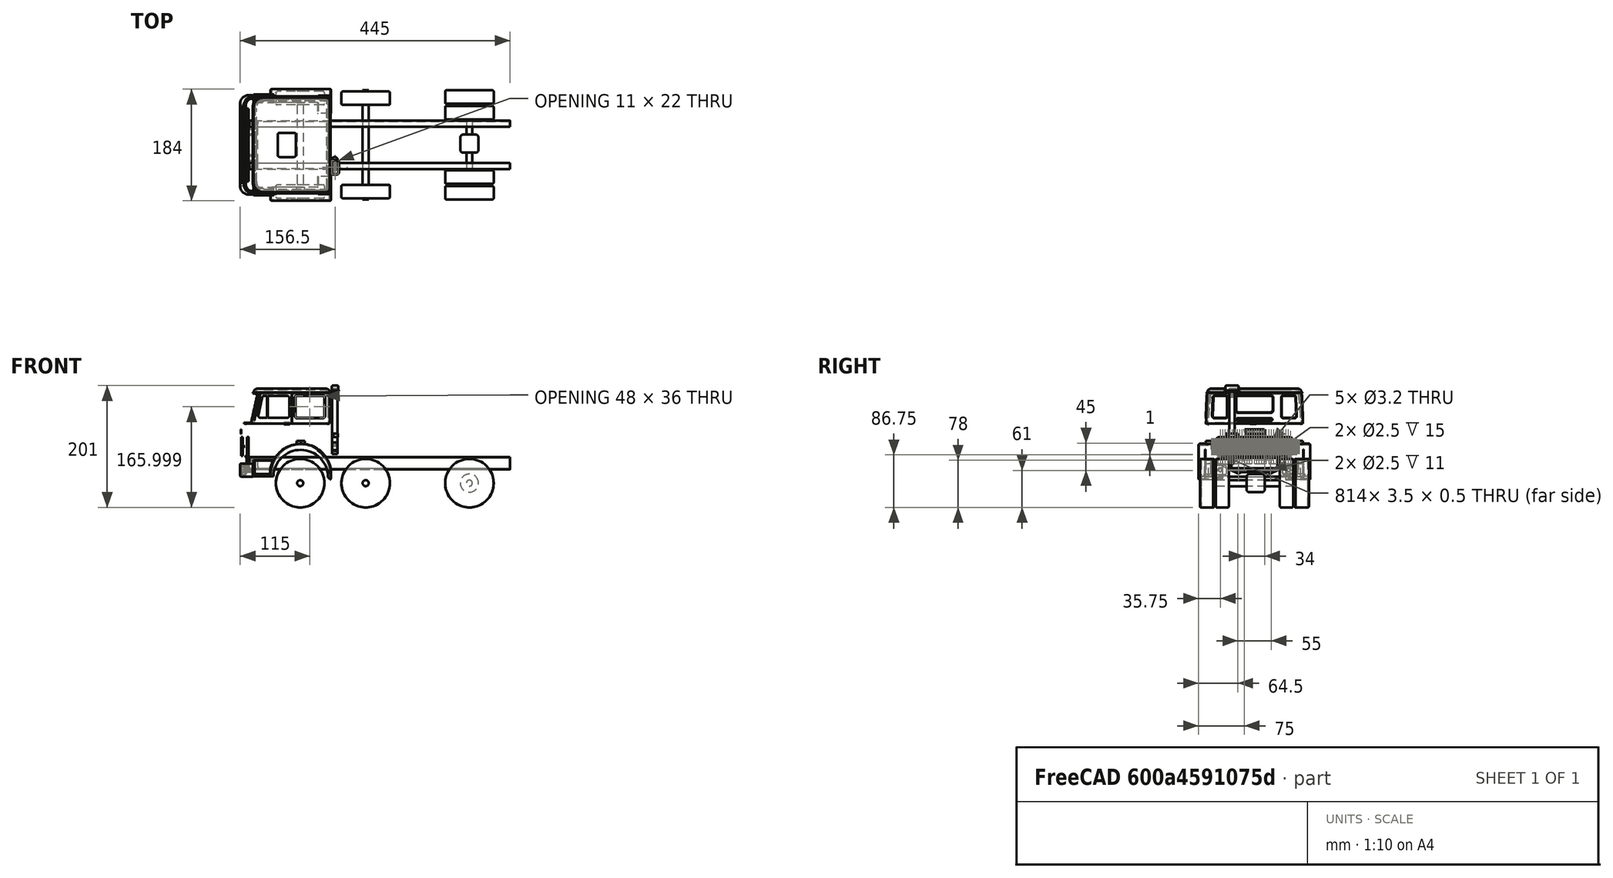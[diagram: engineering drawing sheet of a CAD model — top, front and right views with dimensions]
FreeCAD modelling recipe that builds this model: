
FCSTD DOCUMENT  (FreeCAD 0.20R)
Label: Cab-EMPTY-08a-splitted
License: CC-BY 3.0
LicenseURL: http://creativecommons.org/licenses/by/3.0/
objects: Part::Box×172, Part::Cut×85, Part::MultiFuse×76, Part::Fillet×54, Part::Cylinder×51, Part::Extrusion×7, Part::Mirroring×5, Part::Part2DObjectPython×5, Part::Feature×3, Part::Chamfer×2, Part::Torus×2
note: 462 computed .brp shape members not serialized (recipe doc carries the construction recipe); baked Part::Feature solids carry a one-line shape summary decoded from their .brp

FEATURE [Part::Cut] Cut
  Refine = true
FEATURE [Part::MultiFuse] Fusion
  Refine = true
FEATURE [Part::Cut] Cut001  label="cab"
  Base = -> Cut
  Refine = true
  Tool = -> Fusion
FEATURE [Part::Box] Box  label="Cube"
  AttacherType = Attacher::AttachEngine3D
  Height = 64
  Length = 150
  Placement = pos=(0,-1,-4) rot=(0,0,1;0rad)
  Width = 170
FEATURE [Part::Box] Box001  label="Cube001"
  AttacherType = Attacher::AttachEngine3D
  Height = 64
  Length = 150
  Placement = pos=(0,-1,60) rot=(0,0,1;0rad)
  Width = 170
FEATURE [Part::MultiFuse] Fusion001
  Refine = true
FEATURE [Part::Cut] Cut002
  Refine = true
FEATURE [Part::Cut] Cut004
  Base = -> Cut001
  Refine = true
  Tool = -> Box
FEATURE [Part::Box] Box002  label="Cube002"
  AttacherType = Attacher::AttachEngine3D
  Height = 2
  Length = 10
  Placement = pos=(70,7,59) rot=(0,0,1;0rad)
  Width = 1
FEATURE [Part::Box] Box003  label="Cube003"
  AttacherType = Attacher::AttachEngine3D
  Height = 2
  Length = 10
  Placement = pos=(70,160,59.5) rot=(0,0,1;0rad)
  Width = 1
FEATURE [Part::Box] Box004  label="Cube004"
  AttacherType = Attacher::AttachEngine3D
  Height = 2
  Length = 1
  Placement = pos=(142,77,59.5) rot=(0,0,1;0rad)
  Width = 10
FEATURE [Part::Box] Box005  label="Cube005"
  AttacherType = Attacher::AttachEngine3D
  Height = 2
  Length = 1
  Placement = pos=(7,77,59.5) rot=(0,0,1;0rad)
  Width = 10
FEATURE [Part::MultiFuse] Fusion002
  Refine = true
  Shapes = -> [Box002,Box005,Box004,Box003]
FEATURE [Part::MultiFuse] Fusion003
  Refine = true
  Shapes = -> [Cut004,Fusion002]
FEATURE [Part::Chamfer] Chamfer001
  Base = -> Fusion003
  Edges = 3 edges r=0.5: [Edge92,Edge231,Edge238]
FEATURE [Part::Chamfer] Chamfer
  Base = -> Chamfer001
  Edges = 1 edges r=0.5: [Edge236]
FEATURE [Part::Box] Box006  label="Cube006"
  AttacherType = Attacher::AttachEngine3D
  Height = 48
  Length = 30
  Placement = pos=(0,4,61.5) rot=(0,0,1;0rad)
  Width = 170
FEATURE [Part::Box] Box007  label="Cube007"
  AttacherType = Attacher::AttachEngine3D
  Height = 59
  Length = 15
  Placement = pos=(15.66,0,60) rot=(0,1,0;0.218166rad)
  Width = 180
FEATURE [Part::Cut] Cut006
  Base = -> Box006
  Refine = true
  Tool = -> Box007
FEATURE [Part::Fillet] Fillet
  Base = -> Cut006
  Edges = 1 edges r=1: [Edge9]
FEATURE [Part::Fillet] Fillet001
  Base = -> Fillet
  Edges = 1 edges r=1: [Edge8]
FEATURE [Part::Cut] Cut007
  Base = -> Chamfer
  Refine = true
  Tool = -> Fillet001
FEATURE [Part::Box] Box008  label="Cube008"
  AttacherType = Attacher::AttachEngine3D
  Height = 36
  Length = 36
  Placement = pos=(43,2,70) rot=(0,0,1;0rad)
  Width = 180
FEATURE [Part::Fillet] Fillet002
  Base = -> Box008
  Edges = 2 edges r=3: [Edge6,Edge8]
FEATURE [Part::Cut] Cut008
  Base = -> Cut007
  Refine = true
  Tool = -> Fillet002
FEATURE [Part::Box] Box009  label="Cube009"
  AttacherType = Attacher::AttachEngine3D
  Height = 36
  Length = 48
  Placement = pos=(89,2,70) rot=(0,0,1;0rad)
  Width = 180
FEATURE [Part::Fillet] Fillet003
  Base = -> Box009
  Edges = 4 edges r=3: [Edge2,Edge4,Edge6,Edge8]
FEATURE [Part::Cut] Cut009
  Base = -> Cut008
  Refine = true
  Tool = -> Fillet003
FEATURE [Part::Cut] Cut010
  Placement = pos=(0,1,1) rot=(0,0,1;0rad)
  Refine = true
FEATURE [Part::Fillet] Fillet004
  Base = -> Cut010
  Edges = 4 edges r=3: [Edge5,Edge7,Edge8,Edge11]
  Placement = pos=(-32.5,14,69) rot=(0,0,1;0rad)
FEATURE [Part::Cut] Cut011
  Placement = pos=(0,1,1) rot=(0,0,1;0rad)
  Refine = true
FEATURE [Part::Fillet] Fillet005
  Base = -> Cut011
  Edges = 4 edges r=3: [Edge5,Edge7,Edge8,Edge11]
  Placement = pos=(-32.5,14,69) rot=(0,0,1;0rad)
FEATURE [Part::Mirroring] Part__Mirroring  label="Fillet005 (Mirror #1)"
  Base = (0,0,0)
  Normal = (0,1,0)
  Placement = pos=(0,168,0) rot=(0,0,1;0rad)
  Source = -> Fillet005
FEATURE [Part::MultiFuse] Fusion004
  Refine = true
  Shapes = -> [Fillet004,Part__Mirroring]
FEATURE [Part::Cut] Cut012
  Base = -> Cut009
  Refine = true
  Tool = -> Fusion004
FEATURE [Part::Box] Box010  label="Cube010"
  AttacherType = Attacher::AttachEngine3D
  Height = 27
  Length = 10
  Placement = pos=(139,54,79) rot=(0,0,1;0rad)
  Width = 60
FEATURE [Part::Fillet] Fillet006
  Base = -> Box010
  Edges = 4 edges r=3: [Edge9,Edge10,Edge11,Edge12]
FEATURE [Part::Cut] Cut013
  Base = -> Cut012
  Refine = true
  Tool = -> Fillet006
FEATURE [Part::Box] Box011  label="Cube011"
  AttacherType = Attacher::AttachEngine3D
  Height = 36
  Length = 15
  Placement = pos=(27,0,70) rot=(0,0,1;0rad)
  Width = 180
FEATURE [Part::Box] Box012  label="Cube012"
  AttacherType = Attacher::AttachEngine3D
  Height = 50
  Length = 15
  Placement = pos=(11.85,0,70) rot=(0,1,0;0.20944rad)
  Width = 180
FEATURE [Part::Cut] Cut014
  Base = -> Box011
  Refine = true
  Tool = -> Box012
FEATURE [Part::Fillet] Fillet007
  Base = -> Cut014
  Edges = 2 edges r=3: [Edge9,Edge12]
FEATURE [Part::Cut] Cut015  label="upper"
  Base = -> Cut013
  Refine = true
  Tool = -> Fillet007
FEATURE [Part::Cylinder] Cylinder
  Angle = 360
  AttacherType = Attacher::AttachEngine3D
  FirstAngle = 0
  Height = 15
  Radius = 2.7
  SecondAngle = 0
FEATURE [Part::Cylinder] Cylinder001
  Angle = 360
  AttacherType = Attacher::AttachEngine3D
  FirstAngle = 0
  Height = 15
  Radius = 2.7
  SecondAngle = 0
FEATURE [Part::Fillet] Fillet008
  Base = -> Cylinder
  Edges = 2 edges r=2: [Edge1,Edge3]
  Placement = pos=(152.5,151,39) rot=(1,0,0;1.5708rad)
FEATURE [Part::Cylinder] Cylinder002
  Angle = 360
  AttacherType = Attacher::AttachEngine3D
  FirstAngle = 0
  Height = 15
  Radius = 2.7
  SecondAngle = 0
FEATURE [Part::Cylinder] Cylinder003
  Angle = 360
  AttacherType = Attacher::AttachEngine3D
  FirstAngle = 0
  Height = 60
  Radius = 3.7
  SecondAngle = 0
FEATURE [Part::Fillet] Fillet009
  Base = -> Cylinder003
  Edges = 2 edges r=2: [Edge1,Edge3]
  Placement = pos=(149,114,67) rot=(1,0,0;1.5708rad)
FEATURE [Part::Fillet] Fillet011
  Base = -> Cylinder001
  Edges = 2 edges r=2: [Edge1,Edge3]
  Placement = pos=(152.5,151,31) rot=(1,0,0;1.5708rad)
FEATURE [Part::Fillet] Fillet012
  Base = -> Cylinder002
  Edges = 2 edges r=2: [Edge1,Edge3]
  Placement = pos=(152.5,31,31) rot=(1,0,0;1.5708rad)
FEATURE [Part::Cylinder] Cylinder004
  Angle = 360
  AttacherType = Attacher::AttachEngine3D
  FirstAngle = 0
  Height = 15
  Radius = 2.7
  SecondAngle = 0
FEATURE [Part::Fillet] Fillet010
  Base = -> Cylinder004
  Edges = 2 edges r=2: [Edge1,Edge3]
  Placement = pos=(152.5,31,39) rot=(1,0,0;1.5708rad)
FEATURE [Part::MultiFuse] Fusion006
  Refine = true
  Shapes = -> [Fillet008,Fillet010,Fillet011,Fillet012]
FEATURE [Part::Cut] Cut016
  Base = -> Cut015
  Refine = true
  Tool = -> Fillet009
FEATURE [Part::MultiFuse] Fusion007
  Refine = true
  Shapes = -> [Box001,Fusion006,Fusion001]
FEATURE [Part::Cut] Cut017  label="cab-lower"
  Base = -> Cut002
  Refine = true
  Tool = -> Fusion007
FEATURE [Part::Feature] Face
  shape: bbox 2e-07 x 4.854 x 39.85 mm, 1 faces, 0 solids (baked)
FEATURE [Part::Extrusion] Extrude
  Base = -> Face
  Dir = (1,0,0)
  DirMode = 0
  FaceMakerClass = Part::FaceMakerExtrusion
  LengthFwd = 0
  LengthRev = 0
  Placement = pos=(-0.5,0,0) rot=(0,0,1;0rad)
  Solid = false
  Symmetric = false
FEATURE [Part::MultiFuse] Fusion008
  Refine = true
  Shapes = -> [Cut016,Extrude]
FEATURE [Part::Feature] Face001
  shape: bbox 2e-07 x 4.854 x 39.85 mm, 1 faces, 0 solids (baked)
FEATURE [Part::Extrusion] Extrude001
  Base = -> Face001
  Dir = (1,0,0)
  DirMode = 0
  FaceMakerClass = Part::FaceMakerExtrusion
  LengthFwd = 0
  LengthRev = 0
  Placement = pos=(-0.5,0,0) rot=(0,0,1;0rad)
  Solid = false
  Symmetric = false
FEATURE [Part::Mirroring] Part__Mirroring001  label="Extrude001 (Mirror #2)"
  Base = (0,0,0)
  Normal = (0,1,0)
  Placement = pos=(0,168,0) rot=(0,0,1;0rad)
  Source = -> Extrude001
FEATURE [Part::MultiFuse] Fusion009  label="cab-upper"
  Refine = true
  Shapes = -> [Fusion008,Part__Mirroring001]
FEATURE [Part::Box] Box013  label="Cube"
  AttacherType = Attacher::AttachEngine3D
  Height = 60
  Length = 150
  Width = 168
FEATURE [Part::Box] Box014  label="Cube001"
  AttacherType = Attacher::AttachEngine3D
  Height = 21
  Length = 148
  Placement = pos=(0,0,6) rot=(0,0,1;0rad)
  Width = 168
FEATURE [Part::Box] Box015  label="Cube003"
  AttacherType = Attacher::AttachEngine3D
  Height = 21
  Length = 146
  Placement = pos=(2,2,6) rot=(0,0,1;0rad)
  Width = 164
FEATURE [Part::Box] Box016  label="Cube004"
  AttacherType = Attacher::AttachEngine3D
  Height = 60
  Length = 142
  Placement = pos=(4,4,0) rot=(0,0,1;0rad)
  Width = 160
FEATURE [Part::Box] Box017  label="Cube011"
  AttacherType = Attacher::AttachEngine3D
  Height = 27
  Length = 34
  Placement = pos=(20,152,-27) rot=(0,0,1;0rad)
  Width = 16
FEATURE [Part::Box] Box018  label="Cube012"
  AttacherType = Attacher::AttachEngine3D
  Height = 27
  Length = 30
  Placement = pos=(32,152,-54) rot=(0,0,1;0rad)
  Width = 22
FEATURE [Part::Box] Box019  label="Cube013"
  AttacherType = Attacher::AttachEngine3D
  Height = 22
  Length = 31
  Placement = pos=(22,162,-23) rot=(0,0,1;0rad)
  Width = 6
FEATURE [Part::Box] Box020  label="Cube014"
  AttacherType = Attacher::AttachEngine3D
  Height = 22
  Length = 21
  Placement = pos=(-2,2,-27) rot=(0,0,1;0rad)
  Width = 164
FEATURE [Part::Box] Box021  label="Cube015"
  AttacherType = Attacher::AttachEngine3D
  Height = 22
  Length = 35
  Placement = pos=(20,162,-23) rot=(0,0,1;0rad)
  Width = 6
FEATURE [Part::Box] Box022  label="Cube016"
  AttacherType = Attacher::AttachEngine3D
  Height = 22
  Length = 31
  Placement = pos=(22,154,-23) rot=(0,0,1;0rad)
  Width = 8
FEATURE [Part::Box] Box023  label="Cube017"
  AttacherType = Attacher::AttachEngine3D
  Height = 22
  Length = 21
  Placement = pos=(6,8,-27) rot=(0,0,1;0rad)
  Width = 152
FEATURE [Part::Box] Box024  label="Cube018"
  AttacherType = Attacher::AttachEngine3D
  Height = 1
  Length = 128
  Placement = pos=(19,5,111) rot=(0,0,1;0rad)
  Width = 158
FEATURE [Part::Box] Box025  label="Cube019"
  AttacherType = Attacher::AttachEngine3D
  Height = 31
  Length = 2
  Placement = pos=(-44,21,7) rot=(0,0,1;0rad)
  Width = 126
FEATURE [Part::Box] Box026  label="Cube023"
  AttacherType = Attacher::AttachEngine3D
  Height = 7
  Length = 126
  Placement = pos=(20,6,111) rot=(0,0,1;0rad)
  Width = 156
FEATURE [Part::Box] Box035  label="Cube035"
  AttacherType = Attacher::AttachEngine3D
  Height = 29
  Length = 2
  Placement = pos=(-11,22,8) rot=(0,0,1;0rad)
  Width = 124
FEATURE [Part::Box] Box036  label="Cube036"
  AttacherType = Attacher::AttachEngine3D
  Height = 1
  Length = 1
  Placement = pos=(0.5,22,21) rot=(0,0,1;0rad)
  Width = 124
FEATURE [Part::Box] Box037  label="Cube037"
  AttacherType = Attacher::AttachEngine3D
  Height = 1
  Length = 1
  Placement = pos=(0.5,22,23) rot=(0,0,1;0rad)
  Width = 124
FEATURE [Part::Box] Box038  label="Cube038"
  AttacherType = Attacher::AttachEngine3D
  Height = 29
  Length = 1
  Placement = pos=(0,83,8) rot=(0,0,1;0rad)
  Width = 1
FEATURE [Part::Box] Box039  label="Cube039"
  AttacherType = Attacher::AttachEngine3D
  Height = 29
  Length = 1
  Placement = pos=(0,85,8) rot=(0,0,1;0rad)
  Width = 1
FEATURE [Part::Box] Box040  label="Cube040"
  AttacherType = Attacher::AttachEngine3D
  Height = 29
  Length = 1
  Placement = pos=(0,85,8) rot=(0,0,1;0rad)
  Width = 1
FEATURE [Part::Box] Box041  label="Cube041"
  AttacherType = Attacher::AttachEngine3D
  Height = 29
  Length = 1
  Placement = pos=(0,83,8) rot=(0,0,1;0rad)
  Width = 1
FEATURE [Part::Box] Box042  label="Cube042"
  AttacherType = Attacher::AttachEngine3D
  Height = 29
  Length = 1
  Placement = pos=(0,85,8) rot=(0,0,1;0rad)
  Width = 1
FEATURE [Part::Box] Box043  label="Cube043"
  AttacherType = Attacher::AttachEngine3D
  Height = 29
  Length = 1
  Placement = pos=(0,83,8) rot=(0,0,1;0rad)
  Width = 1
FEATURE [Part::Box] Box044  label="Cube044"
  AttacherType = Attacher::AttachEngine3D
  Height = 29
  Length = 1
  Placement = pos=(0,48,8) rot=(0,0,1;0rad)
  Width = 1
FEATURE [Part::Box] Box045  label="Cube045"
  AttacherType = Attacher::AttachEngine3D
  Height = 29
  Length = 1
  Placement = pos=(0,120,8) rot=(0,0,1;0rad)
  Width = 1
FEATURE [Part::Box] Box046  label="Cube046"
  AttacherType = Attacher::AttachEngine3D
  Height = 1
  Length = 1
  Placement = pos=(0,83,22) rot=(0,0,1;0rad)
  Width = 3
FEATURE [Part::Box] Box055  label="Cube055"
  AttacherType = Attacher::AttachEngine3D
  Height = 31
  Length = 1
  Placement = pos=(0,120,7) rot=(0,0,1;0rad)
  Width = 1
FEATURE [Part::Box] Box056  label="Cube056"
  AttacherType = Attacher::AttachEngine3D
  Height = 31
  Length = 1
  Placement = pos=(0,48,7) rot=(0,0,1;0rad)
  Width = 1
FEATURE [Part::Box] Box085  label="Cube085"
  AttacherType = Attacher::AttachEngine3D
  Height = 1
  Length = 30
  Placement = pos=(60,64,117) rot=(0,0,1;0rad)
  Width = 40
FEATURE [Part::Box] Box092  label="Cube092"
  AttacherType = Attacher::AttachEngine3D
  Height = 15
  Length = 10
  Placement = pos=(-2,14,-23.5) rot=(0,0,1;0rad)
  Width = 21
FEATURE [Part::Box] Box093  label="Cube093"
  AttacherType = Attacher::AttachEngine3D
  Height = 15
  Length = 10
  Placement = pos=(-2,14,-23.5) rot=(0,0,1;0rad)
  Width = 21
FEATURE [Part::Box] Box114  label="Cube114"
  AttacherType = Attacher::AttachEngine3D
  Height = 29
  Length = 2
  Placement = pos=(-11,22,8) rot=(0,0,1;0rad)
  Width = 124
FEATURE [Part::Box] Box115  label="Cube115"
  AttacherType = Attacher::AttachEngine3D
  Height = 35
  Length = 2
  Placement = pos=(0,19,5) rot=(0,0,1;0rad)
  Width = 130
FEATURE [Part::Box] Box116  label="Cube116"
  AttacherType = Attacher::AttachEngine3D
  Height = 29
  Length = 0.5
  Placement = pos=(1.5,26,8) rot=(0,0,1;0rad)
  Width = 0.5
FEATURE [Part::Box] Box117  label="Cube117"
  AttacherType = Attacher::AttachEngine3D
  Height = 29
  Length = 0.5
  Placement = pos=(1.5,30,8) rot=(0,0,1;0rad)
  Width = 0.5
FEATURE [Part::Box] Box118  label="Cube118"
  AttacherType = Attacher::AttachEngine3D
  Height = 29
  Length = 0.5
  Placement = pos=(1.5,34,8) rot=(0,0,1;0rad)
  Width = 0.5
FEATURE [Part::Box] Box119  label="Cube119"
  AttacherType = Attacher::AttachEngine3D
  Height = 29
  Length = 0.5
  Placement = pos=(1.5,38,8) rot=(0,0,1;0rad)
  Width = 0.5
FEATURE [Part::Box] Box120  label="Cube120"
  AttacherType = Attacher::AttachEngine3D
  Height = 29
  Length = 0.5
  Placement = pos=(1.5,42,8) rot=(0,0,1;0rad)
  Width = 0.5
FEATURE [Part::Box] Box121  label="Cube121"
  AttacherType = Attacher::AttachEngine3D
  Height = 29
  Length = 0.5
  Placement = pos=(1.5,46,8) rot=(0,0,1;0rad)
  Width = 0.5
FEATURE [Part::Box] Box122  label="Cube122"
  AttacherType = Attacher::AttachEngine3D
  Height = 0.5
  Length = 0.5
  Placement = pos=(1.5,26,8) rot=(0,0,1;0rad)
  Width = 20
FEATURE [Part::Box] Box123  label="Cube123"
  AttacherType = Attacher::AttachEngine3D
  Height = 0.5
  Length = 0.5
  Placement = pos=(1.5,26,9) rot=(0,0,1;0rad)
  Width = 20
FEATURE [Part::Box] Box124  label="Cube124"
  AttacherType = Attacher::AttachEngine3D
  Height = 0.5
  Length = 0.5
  Placement = pos=(1.5,26,10) rot=(0,0,1;0rad)
  Width = 20
FEATURE [Part::Box] Box125  label="Cube125"
  AttacherType = Attacher::AttachEngine3D
  Height = 0.5
  Length = 0.5
  Placement = pos=(1.5,26,11) rot=(0,0,1;0rad)
  Width = 20
FEATURE [Part::Box] Box126  label="Cube126"
  AttacherType = Attacher::AttachEngine3D
  Height = 0.5
  Length = 0.5
  Placement = pos=(1.5,26,12) rot=(0,0,1;0rad)
  Width = 20
FEATURE [Part::Box] Box127  label="Cube127"
  AttacherType = Attacher::AttachEngine3D
  Height = 0.5
  Length = 0.5
  Placement = pos=(1.5,26,13) rot=(0,0,1;0rad)
  Width = 20
FEATURE [Part::Box] Box128  label="Cube128"
  AttacherType = Attacher::AttachEngine3D
  Height = 0.5
  Length = 0.5
  Placement = pos=(1.5,26,14) rot=(0,0,1;0rad)
  Width = 20
FEATURE [Part::Box] Box129  label="Cube129"
  AttacherType = Attacher::AttachEngine3D
  Height = 0.5
  Length = 0.5
  Placement = pos=(1.5,26,15) rot=(0,0,1;0rad)
  Width = 20
FEATURE [Part::Box] Box130  label="Cube130"
  AttacherType = Attacher::AttachEngine3D
  Height = 0.5
  Length = 0.5
  Placement = pos=(1.5,26,16) rot=(0,0,1;0rad)
  Width = 20
FEATURE [Part::Box] Box131  label="Cube131"
  AttacherType = Attacher::AttachEngine3D
  Height = 0.5
  Length = 0.5
  Placement = pos=(1.5,26,17) rot=(0,0,1;0rad)
  Width = 20
FEATURE [Part::Box] Box132  label="Cube132"
  AttacherType = Attacher::AttachEngine3D
  Height = 0.5
  Length = 0.5
  Placement = pos=(1.5,26,18) rot=(0,0,1;0rad)
  Width = 20
FEATURE [Part::Box] Box133  label="Cube133"
  AttacherType = Attacher::AttachEngine3D
  Height = 0.5
  Length = 0.5
  Placement = pos=(1.5,26,19) rot=(0,0,1;0rad)
  Width = 20
FEATURE [Part::Box] Box134  label="Cube134"
  AttacherType = Attacher::AttachEngine3D
  Height = 0.5
  Length = 0.5
  Placement = pos=(1.5,26,20) rot=(0,0,1;0rad)
  Width = 20
FEATURE [Part::Box] Box135  label="Cube135"
  AttacherType = Attacher::AttachEngine3D
  Height = 0.5
  Length = 0.5
  Placement = pos=(1.5,26,21) rot=(0,0,1;0rad)
  Width = 20
FEATURE [Part::Box] Box136  label="Cube136"
  AttacherType = Attacher::AttachEngine3D
  Height = 0.5
  Length = 0.5
  Placement = pos=(1.5,26,22) rot=(0,0,1;0rad)
  Width = 20
FEATURE [Part::Box] Box137  label="Cube137"
  AttacherType = Attacher::AttachEngine3D
  Height = 0.5
  Length = 0.5
  Placement = pos=(1.5,26,19) rot=(0,0,1;0rad)
  Width = 20
FEATURE [Part::Box] Box138  label="Cube138"
  AttacherType = Attacher::AttachEngine3D
  Height = 0.5
  Length = 0.5
  Placement = pos=(1.5,26,11) rot=(0,0,1;0rad)
  Width = 20
FEATURE [Part::Box] Box139  label="Cube139"
  AttacherType = Attacher::AttachEngine3D
  Height = 0.5
  Length = 0.5
  Placement = pos=(1.5,26,18) rot=(0,0,1;0rad)
  Width = 20
FEATURE [Part::Box] Box140  label="Cube140"
  AttacherType = Attacher::AttachEngine3D
  Height = 0.5
  Length = 0.5
  Placement = pos=(1.5,26,12) rot=(0,0,1;0rad)
  Width = 20
FEATURE [Part::Box] Box141  label="Cube141"
  AttacherType = Attacher::AttachEngine3D
  Height = 0.5
  Length = 0.5
  Placement = pos=(1.5,26,15) rot=(0,0,1;0rad)
  Width = 20
FEATURE [Part::Box] Box142  label="Cube142"
  AttacherType = Attacher::AttachEngine3D
  Height = 0.5
  Length = 0.5
  Placement = pos=(1.5,26,8) rot=(0,0,1;0rad)
  Width = 20
FEATURE [Part::Box] Box143  label="Cube143"
  AttacherType = Attacher::AttachEngine3D
  Height = 0.5
  Length = 0.5
  Placement = pos=(1.5,26,21) rot=(0,0,1;0rad)
  Width = 20
FEATURE [Part::Box] Box144  label="Cube144"
  AttacherType = Attacher::AttachEngine3D
  Height = 0.5
  Length = 0.5
  Placement = pos=(1.5,26,10) rot=(0,0,1;0rad)
  Width = 20
FEATURE [Part::Box] Box145  label="Cube145"
  AttacherType = Attacher::AttachEngine3D
  Height = 0.5
  Length = 0.5
  Placement = pos=(1.5,26,14) rot=(0,0,1;0rad)
  Width = 20
FEATURE [Part::Box] Box146  label="Cube146"
  AttacherType = Attacher::AttachEngine3D
  Height = 0.5
  Length = 0.5
  Placement = pos=(1.5,26,13) rot=(0,0,1;0rad)
  Width = 20
FEATURE [Part::Box] Box147  label="Cube147"
  AttacherType = Attacher::AttachEngine3D
  Height = 0.5
  Length = 0.5
  Placement = pos=(1.5,26,17) rot=(0,0,1;0rad)
  Width = 20
FEATURE [Part::Box] Box148  label="Cube148"
  AttacherType = Attacher::AttachEngine3D
  Height = 0.5
  Length = 0.5
  Placement = pos=(1.5,26,22) rot=(0,0,1;0rad)
  Width = 20
FEATURE [Part::Box] Box149  label="Cube149"
  AttacherType = Attacher::AttachEngine3D
  Height = 0.5
  Length = 0.5
  Placement = pos=(1.5,26,20) rot=(0,0,1;0rad)
  Width = 20
FEATURE [Part::Box] Box150  label="Cube150"
  AttacherType = Attacher::AttachEngine3D
  Height = 0.5
  Length = 0.5
  Placement = pos=(1.5,26,9) rot=(0,0,1;0rad)
  Width = 20
FEATURE [Part::Box] Box151  label="Cube151"
  AttacherType = Attacher::AttachEngine3D
  Height = 0.5
  Length = 0.5
  Placement = pos=(1.5,26,16) rot=(0,0,1;0rad)
  Width = 20
FEATURE [Part::Box] Box152  label="Cube152"
  AttacherType = Attacher::AttachEngine3D
  Height = 29
  Length = 0.5
  Placement = pos=(1.5,30,8) rot=(0,0,1;0rad)
  Width = 0.5
FEATURE [Part::Box] Box153  label="Cube153"
  AttacherType = Attacher::AttachEngine3D
  Height = 29
  Length = 0.5
  Placement = pos=(1.5,42,8) rot=(0,0,1;0rad)
  Width = 0.5
FEATURE [Part::Box] Box154  label="Cube154"
  AttacherType = Attacher::AttachEngine3D
  Height = 29
  Length = 0.5
  Placement = pos=(1.5,26,8) rot=(0,0,1;0rad)
  Width = 0.5
FEATURE [Part::Box] Box155  label="Cube155"
  AttacherType = Attacher::AttachEngine3D
  Height = 29
  Length = 0.5
  Placement = pos=(1.5,38,8) rot=(0,0,1;0rad)
  Width = 0.5
FEATURE [Part::Box] Box156  label="Cube156"
  AttacherType = Attacher::AttachEngine3D
  Height = 29
  Length = 0.5
  Placement = pos=(1.5,34,8) rot=(0,0,1;0rad)
  Width = 0.5
FEATURE [Part::Box] Box157  label="Cube157"
  AttacherType = Attacher::AttachEngine3D
  Height = 29
  Length = 0.5
  Placement = pos=(1.5,46,8) rot=(0,0,1;0rad)
  Width = 0.5
FEATURE [Part::Box] Box158  label="Cube158"
  AttacherType = Attacher::AttachEngine3D
  Height = 29
  Length = 0.5
  Placement = pos=(1.5,30,8) rot=(0,0,1;0rad)
  Width = 0.5
FEATURE [Part::Box] Box159  label="Cube159"
  AttacherType = Attacher::AttachEngine3D
  Height = 29
  Length = 0.5
  Placement = pos=(1.5,42,8) rot=(0,0,1;0rad)
  Width = 0.5
FEATURE [Part::Box] Box160  label="Cube160"
  AttacherType = Attacher::AttachEngine3D
  Height = 29
  Length = 0.5
  Placement = pos=(1.5,26,8) rot=(0,0,1;0rad)
  Width = 0.5
FEATURE [Part::Box] Box161  label="Cube161"
  AttacherType = Attacher::AttachEngine3D
  Height = 29
  Length = 0.5
  Placement = pos=(1.5,38,8) rot=(0,0,1;0rad)
  Width = 0.5
FEATURE [Part::Box] Box162  label="Cube162"
  AttacherType = Attacher::AttachEngine3D
  Height = 29
  Length = 0.5
  Placement = pos=(1.5,34,8) rot=(0,0,1;0rad)
  Width = 0.5
FEATURE [Part::Box] Box163  label="Cube163"
  AttacherType = Attacher::AttachEngine3D
  Height = 29
  Length = 0.5
  Placement = pos=(1.5,46,8) rot=(0,0,1;0rad)
  Width = 0.5
FEATURE [Part::Box] Box164  label="Cube164"
  AttacherType = Attacher::AttachEngine3D
  Height = 29
  Length = 0.5
  Placement = pos=(1.5,46,8) rot=(0,0,1;0rad)
  Width = 0.5
FEATURE [Part::Box] Box165  label="Cube165"
  AttacherType = Attacher::AttachEngine3D
  Height = 29
  Length = 0.5
  Placement = pos=(1.5,30,8) rot=(0,0,1;0rad)
  Width = 0.5
FEATURE [Part::Box] Box166  label="Cube166"
  AttacherType = Attacher::AttachEngine3D
  Height = 29
  Length = 0.5
  Placement = pos=(1.5,34,8) rot=(0,0,1;0rad)
  Width = 0.5
FEATURE [Part::Box] Box167  label="Cube167"
  AttacherType = Attacher::AttachEngine3D
  Height = 29
  Length = 0.5
  Placement = pos=(1.5,42,8) rot=(0,0,1;0rad)
  Width = 0.5
FEATURE [Part::Box] Box168  label="Cube168"
  AttacherType = Attacher::AttachEngine3D
  Height = 29
  Length = 0.5
  Placement = pos=(1.5,26,8) rot=(0,0,1;0rad)
  Width = 0.5
FEATURE [Part::Box] Box169  label="Cube169"
  AttacherType = Attacher::AttachEngine3D
  Height = 29
  Length = 0.5
  Placement = pos=(1.5,38,8) rot=(0,0,1;0rad)
  Width = 0.5
FEATURE [Part::Box] Box170  label="Cube170"
  AttacherType = Attacher::AttachEngine3D
  Height = 29
  Length = 0.5
  Placement = pos=(1.5,30,8) rot=(0,0,1;0rad)
  Width = 0.5
FEATURE [Part::Box] Box171  label="Cube171"
  AttacherType = Attacher::AttachEngine3D
  Height = 29
  Length = 0.5
  Placement = pos=(1.5,42,8) rot=(0,0,1;0rad)
  Width = 0.5
FEATURE [Part::Box] Box172  label="Cube172"
  AttacherType = Attacher::AttachEngine3D
  Height = 29
  Length = 0.5
  Placement = pos=(1.5,38,8) rot=(0,0,1;0rad)
  Width = 0.5
FEATURE [Part::Box] Box173  label="Cube173"
  AttacherType = Attacher::AttachEngine3D
  Height = 29
  Length = 0.5
  Placement = pos=(1.5,46,8) rot=(0,0,1;0rad)
  Width = 0.5
FEATURE [Part::Box] Box174  label="Cube174"
  AttacherType = Attacher::AttachEngine3D
  Height = 29
  Length = 0.5
  Placement = pos=(1.5,26,8) rot=(0,0,1;0rad)
  Width = 0.5
FEATURE [Part::Box] Box175  label="Cube175"
  AttacherType = Attacher::AttachEngine3D
  Height = 29
  Length = 0.5
  Placement = pos=(1.5,34,8) rot=(0,0,1;0rad)
  Width = 0.5
FEATURE [Part::Box] Box176  label="Cube176"
  AttacherType = Attacher::AttachEngine3D
  Height = 29
  Length = 0.5
  Placement = pos=(1.5,38,8) rot=(0,0,1;0rad)
  Width = 0.5
FEATURE [Part::Box] Box177  label="Cube177"
  AttacherType = Attacher::AttachEngine3D
  Height = 29
  Length = 0.5
  Placement = pos=(1.5,42,8) rot=(0,0,1;0rad)
  Width = 0.5
FEATURE [Part::Box] Box178  label="Cube178"
  AttacherType = Attacher::AttachEngine3D
  Height = 29
  Length = 0.5
  Placement = pos=(1.5,30,8) rot=(0,0,1;0rad)
  Width = 0.5
FEATURE [Part::Box] Box179  label="Cube179"
  AttacherType = Attacher::AttachEngine3D
  Height = 29
  Length = 0.5
  Placement = pos=(1.5,46,8) rot=(0,0,1;0rad)
  Width = 0.5
FEATURE [Part::Box] Box180  label="Cube180"
  AttacherType = Attacher::AttachEngine3D
  Height = 29
  Length = 0.5
  Placement = pos=(1.5,26,8) rot=(0,0,1;0rad)
  Width = 0.5
FEATURE [Part::Box] Box181  label="Cube181"
  AttacherType = Attacher::AttachEngine3D
  Height = 29
  Length = 0.5
  Placement = pos=(1.5,34,8) rot=(0,0,1;0rad)
  Width = 0.5
FEATURE [Part::Box] Box182  label="Cube182"
  AttacherType = Attacher::AttachEngine3D
  Height = 29
  Length = 0.5
  Placement = pos=(1.5,42,8) rot=(0,0,1;0rad)
  Width = 0.5
FEATURE [Part::Box] Box183  label="Cube183"
  AttacherType = Attacher::AttachEngine3D
  Height = 29
  Length = 0.5
  Placement = pos=(1.5,46,8) rot=(0,0,1;0rad)
  Width = 0.5
FEATURE [Part::Box] Box184  label="Cube184"
  AttacherType = Attacher::AttachEngine3D
  Height = 29
  Length = 0.5
  Placement = pos=(1.5,26,8) rot=(0,0,1;0rad)
  Width = 0.5
FEATURE [Part::Box] Box185  label="Cube185"
  AttacherType = Attacher::AttachEngine3D
  Height = 29
  Length = 0.5
  Placement = pos=(1.5,30,8) rot=(0,0,1;0rad)
  Width = 0.5
FEATURE [Part::Box] Box186  label="Cube186"
  AttacherType = Attacher::AttachEngine3D
  Height = 29
  Length = 0.5
  Placement = pos=(1.5,38,8) rot=(0,0,1;0rad)
  Width = 0.5
FEATURE [Part::Box] Box187  label="Cube187"
  AttacherType = Attacher::AttachEngine3D
  Height = 29
  Length = 0.5
  Placement = pos=(1.5,34,8) rot=(0,0,1;0rad)
  Width = 0.5
FEATURE [Part::Box] Box188  label="Cube188"
  AttacherType = Attacher::AttachEngine3D
  Height = 5.8
  Length = 13.6
  Placement = pos=(91.2,5,26) rot=(0,0,1;0rad)
  Width = 10
FEATURE [Part::Box] Box192  label="Cube192"
  AttacherType = Attacher::AttachEngine3D
  Height = 5.8
  Length = 13.6
  Placement = pos=(91.2,153,26) rot=(0,0,1;0rad)
  Width = 10
FEATURE [Part::Box] Box202  label="Cube202"
  AttacherType = Attacher::AttachEngine3D
  Height = 2
  Length = 119.6
  Placement = pos=(23.2,9.2,109) rot=(0,0,1;0rad)
  Width = 149.6
FEATURE [Part::Box] Box203  label="Cube203"
  AttacherType = Attacher::AttachEngine3D
  Height = 7
  Length = 116
  Placement = pos=(25,11,109) rot=(0,0,1;0rad)
  Width = 146
FEATURE [Part::Box] Box204  label="Cube204"
  AttacherType = Attacher::AttachEngine3D
  Height = 10
  Length = 10
  Placement = pos=(140.3,-7,-39.5) rot=(0,-1,0;0.785398rad)
  Width = 40
FEATURE [Part::Box] Box205  label="Cube205"
  AttacherType = Attacher::AttachEngine3D
  Height = 10
  Length = 10
  Placement = pos=(140.3,135,-39.5) rot=(0,-1,0;0.785398rad)
  Width = 40
FEATURE [Part::Box] Box206  label="Cube206"
  AttacherType = Attacher::AttachEngine3D
  Height = 10
  Length = 11
  Placement = pos=(149,37,113) rot=(0,0,1;0rad)
  Width = 22
FEATURE [Part::Box] Box207  label="Cube207"
  AttacherType = Attacher::AttachEngine3D
  Height = 1
  Length = 13
  Placement = pos=(148,36,114) rot=(0,0,1;0rad)
  Width = 24
FEATURE [Part::Box] Box208  label="Cube208"
  AttacherType = Attacher::AttachEngine3D
  Height = 0.5
  Length = 2
  Placement = pos=(32.54,0,0) rot=(0,0,-1;0.191986rad)
  Width = 9
FEATURE [Part::Box] Box209  label="Cube209"
  AttacherType = Attacher::AttachEngine3D
  Height = 0.5
  Length = 35
  Width = 8
FEATURE [Part::Box] Box210  label="Cube210"
  AttacherType = Attacher::AttachEngine3D
  Height = 6
  Length = 2
  Placement = pos=(148,37,38) rot=(0,0,1;0rad)
  Width = 20
FEATURE [Part::Box] Box211  label="Cube211"
  AttacherType = Attacher::AttachEngine3D
  Height = 6
  Length = 2
  Placement = pos=(150,37,38) rot=(0,0,1;0rad)
  Width = 20
FEATURE [Part::Box] Box212  label="Cube212"
  AttacherType = Attacher::AttachEngine3D
  Height = 6
  Length = 3.5
  Placement = pos=(146,43,104) rot=(0,0,1;0rad)
  Width = 8
FEATURE [Part::Box] Box213  label="Cube213"
  AttacherType = Attacher::AttachEngine3D
  Height = 6
  Length = 4
  Placement = pos=(149.5,43,104) rot=(0,0,1;0rad)
  Width = 8
FEATURE [Part::Box] Box214  label="Cube206"
  AttacherType = Attacher::AttachEngine3D
  Height = 0.5
  Length = 34.5
  Width = 8
FEATURE [Part::Box] Box215  label="Cube207"
  AttacherType = Attacher::AttachEngine3D
  Height = 0.5
  Length = 2
  Placement = pos=(-2,0,0) rot=(0,0,-1;0.191986rad)
  Width = 9
FEATURE [Part::Box] Box216  label="Cube210"
  AttacherType = Attacher::AttachEngine3D
  Height = 0.5
  Length = 2
  Placement = pos=(-2,0,0) rot=(0,0,-1;0.191986rad)
  Width = 9
FEATURE [Part::Box] Box217  label="Cube211"
  AttacherType = Attacher::AttachEngine3D
  Height = 0.5
  Length = 2
  Placement = pos=(33.4,0,0) rot=(0,0,-1;0.191986rad)
  Width = 9
FEATURE [Part::Box] Box218  label="Cube212"
  AttacherType = Attacher::AttachEngine3D
  Height = 0.5
  Length = 35
  Width = 8
FEATURE [Part::Box] Box219  label="Cube213"
  AttacherType = Attacher::AttachEngine3D
  Height = 0.5
  Length = 2
  Placement = pos=(-2,0,0) rot=(0,0,-1;0.191986rad)
  Width = 9
FEATURE [Part::Box] Box220  label="Cube214"
  AttacherType = Attacher::AttachEngine3D
  Height = 0.5
  Length = 2
  Placement = pos=(33.4,0,0) rot=(0,0,-1;0.191986rad)
  Width = 9
FEATURE [Part::Box] Box221  label="Cube215"
  AttacherType = Attacher::AttachEngine3D
  Height = 0.5
  Length = 35
  Width = 8
FEATURE [Part::Box] Box222  label="Cube216"
  AttacherType = Attacher::AttachEngine3D
  Height = 0.5
  Length = 2
  Placement = pos=(-2,0,0) rot=(0,0,-1;0.191986rad)
  Width = 9
FEATURE [Part::Box] Box223  label="Cube217"
  AttacherType = Attacher::AttachEngine3D
  Height = 0.5
  Length = 2
  Placement = pos=(33.4,0,0) rot=(0,0,-1;0.191986rad)
  Width = 9
FEATURE [Part::Box] Box224  label="Cube218"
  AttacherType = Attacher::AttachEngine3D
  Height = 0.5
  Length = 35
  Width = 8
FEATURE [Part::Box] Box225  label="Cube219"
  AttacherType = Attacher::AttachEngine3D
  Height = 0.5
  Length = 2
  Placement = pos=(-2,0,0) rot=(0,0,-1;0.191986rad)
  Width = 9
FEATURE [Part::Box] Box226  label="Cube220"
  AttacherType = Attacher::AttachEngine3D
  Height = 0.5
  Length = 2
  Placement = pos=(33.4,0,0) rot=(0,0,-1;0.191986rad)
  Width = 9
FEATURE [Part::Box] Box227  label="Cube221"
  AttacherType = Attacher::AttachEngine3D
  Height = 0.5
  Length = 35
  Width = 8
FEATURE [Part::Box] Box228  label="Cube222"
  AttacherType = Attacher::AttachEngine3D
  Height = 0.5
  Length = 2
  Placement = pos=(-2,0,0) rot=(0,0,-1;0.191986rad)
  Width = 9
FEATURE [Part::Box] Box229  label="Cube223"
  AttacherType = Attacher::AttachEngine3D
  Height = 0.5
  Length = 2
  Placement = pos=(33.4,0,0) rot=(0,0,-1;0.191986rad)
  Width = 9
FEATURE [Part::Box] Box230  label="Cube224"
  AttacherType = Attacher::AttachEngine3D
  Height = 0.5
  Length = 35
  Width = 8
FEATURE [Part::Box] Box231  label="Cube225"
  AttacherType = Attacher::AttachEngine3D
  Height = 0.5
  Length = 2
  Placement = pos=(-2,0,0) rot=(0,0,-1;0.191986rad)
  Width = 9
FEATURE [Part::Box] Box232  label="Cube226"
  AttacherType = Attacher::AttachEngine3D
  Height = 0.5
  Length = 2
  Placement = pos=(33.4,0,0) rot=(0,0,-1;0.191986rad)
  Width = 9
FEATURE [Part::Box] Box233  label="Cube227"
  AttacherType = Attacher::AttachEngine3D
  Height = 0.5
  Length = 35
  Width = 8
FEATURE [Part::Box] Box234  label="Cube228"
  AttacherType = Attacher::AttachEngine3D
  Height = 0.5
  Length = 2
  Placement = pos=(-2,0,0) rot=(0,0,-1;0.191986rad)
  Width = 9
FEATURE [Part::Box] Box235  label="Cube229"
  AttacherType = Attacher::AttachEngine3D
  Height = 0.5
  Length = 2
  Placement = pos=(33.4,0,0) rot=(0,0,-1;0.191986rad)
  Width = 9
FEATURE [Part::Box] Box236  label="Cube230"
  AttacherType = Attacher::AttachEngine3D
  Height = 0.5
  Length = 35
  Width = 8
FEATURE [Part::Box] Box237  label="Cube231"
  AttacherType = Attacher::AttachEngine3D
  Height = 0.5
  Length = 2
  Placement = pos=(-2,0,0) rot=(0,0,-1;0.191986rad)
  Width = 9
FEATURE [Part::Box] Box238  label="Cube232"
  AttacherType = Attacher::AttachEngine3D
  Height = 0.5
  Length = 2
  Placement = pos=(33.4,0,0) rot=(0,0,-1;0.191986rad)
  Width = 9
FEATURE [Part::Box] Box239  label="Cube233"
  AttacherType = Attacher::AttachEngine3D
  Height = 0.5
  Length = 35
  Width = 8
FEATURE [Part::Box] Box240  label="Cube234"
  AttacherType = Attacher::AttachEngine3D
  Height = 0.5
  Length = 2
  Placement = pos=(-2,0,0) rot=(0,0,-1;0.191986rad)
  Width = 9
FEATURE [Part::Box] Box241  label="Cube235"
  AttacherType = Attacher::AttachEngine3D
  Height = 0.5
  Length = 2
  Placement = pos=(33.4,0,0) rot=(0,0,-1;0.191986rad)
  Width = 9
FEATURE [Part::Box] Box242  label="Cube236"
  AttacherType = Attacher::AttachEngine3D
  Height = 0.5
  Length = 35
  Width = 8
FEATURE [Part::Box] Box243  label="Cube237"
  AttacherType = Attacher::AttachEngine3D
  Height = 0.5
  Length = 2
  Placement = pos=(-2,0,0) rot=(0,0,-1;0.191986rad)
  Width = 9
FEATURE [Part::Box] Box244  label="Cube238"
  AttacherType = Attacher::AttachEngine3D
  Height = 0.5
  Length = 2
  Placement = pos=(33.4,0,0) rot=(0,0,-1;0.191986rad)
  Width = 9
FEATURE [Part::Box] Box245  label="Cube239"
  AttacherType = Attacher::AttachEngine3D
  Height = 0.5
  Length = 32
  Placement = pos=(0.3,0,0.5) rot=(0,0,1;0rad)
  Width = 0.5
FEATURE [Part::Box] Box246  label="Cube240"
  AttacherType = Attacher::AttachEngine3D
  Height = 0.5
  Length = 32
  Placement = pos=(1.9,7.5,0.5) rot=(0,0,1;0rad)
  Width = 0.5
FEATURE [Part::Box] Box247  label="Cube241"
  AttacherType = Attacher::AttachEngine3D
  Height = 0.5
  Length = 13
  Placement = pos=(0,0,0.5) rot=(0,0,1;0rad)
  Width = 5
FEATURE [Part::Box] Box248  label="Cube242"
  AttacherType = Attacher::AttachEngine3D
  Height = 1
  Length = 1
  Placement = pos=(12,0,0) rot=(0,0,-1;0.191986rad)
  Width = 6
FEATURE [Part::Box] Box249  label="Cube243"
  AttacherType = Attacher::AttachEngine3D
  Height = 1
  Length = 1
  Placement = pos=(-1,0,0) rot=(0,0,-1;0.191986rad)
  Width = 6
FEATURE [Part::Box] Box251  label="Cube251"
  AttacherType = Attacher::AttachEngine3D
  Height = 14
  Length = 5
  Placement = pos=(-2,14,-23.5) rot=(0,0,1;0rad)
  Width = 20
FEATURE [Part::Box] Box252  label="Cube252"
  AttacherType = Attacher::AttachEngine3D
  Height = 14
  Length = 0.6
  Placement = pos=(-0.6,14,-23.5) rot=(0,0,1;0rad)
  Width = 20
FEATURE [Part::Box] Box258  label="Cube258"
  AttacherType = Attacher::AttachEngine3D
  Height = 19
  Length = 1
  Placement = pos=(6,127,-26) rot=(0,0,1;0rad)
  Width = 23
FEATURE [Part::Box] Box259  label="Cube259"
  AttacherType = Attacher::AttachEngine3D
  Height = 19
  Length = 1
  Placement = pos=(6,127,-26) rot=(0,0,1;0rad)
  Width = 23
FEATURE [Part::Cut] Cut106  label="cab_tilt_upper"
  Placement = pos=(-2,100,53) rot=(0.57735,-0.57735,-0.57735;2.0944rad)
  Refine = true
FEATURE [Part::Cylinder] Cylinder005
  Angle = 360
  AttacherType = Attacher::AttachEngine3D
  FirstAngle = 0
  Height = 168
  Placement = pos=(98,168,-23) rot=(1,0,0;1.5708rad)
  Radius = 50
  SecondAngle = 0
FEATURE [Part::Cylinder] Cylinder006
  Angle = 198
  AttacherType = Attacher::AttachEngine3D
  FirstAngle = 0
  Height = 22
  Placement = pos=(98,168,-23) rot=(1,0,0;1.5708rad)
  Radius = 50
  SecondAngle = 0
FEATURE [Part::Cylinder] Cylinder007
  Angle = 198
  AttacherType = Attacher::AttachEngine3D
  FirstAngle = 0
  Height = 22
  Placement = pos=(98.7,168,-28) rot=(1,0,0;1.5708rad)
  Radius = 45
  SecondAngle = 0
FEATURE [Part::Cut] Cut021
  Base = -> Cylinder006
  Refine = true
  Tool = -> Cylinder007
FEATURE [Part::Cylinder] Cylinder008
  Angle = 198
  AttacherType = Attacher::AttachEngine3D
  FirstAngle = 0
  Height = 22
  Placement = pos=(98,167,-23) rot=(1,0,0;1.5708rad)
  Radius = 48
  SecondAngle = 0
FEATURE [Part::Cut] Cut022
  Base = -> Cut021
  Placement = pos=(5.48275,6,16.6681) rot=(0,1,0;0.174533rad)
  Refine = true
  Tool = -> Cylinder008
FEATURE [Part::Cut] Cut024
  Base = -> Cut022
  Refine = true
  Tool = -> Box018
FEATURE [Part::Cut] Cut032
  Base = -> Cut022
  Refine = true
  Tool = -> Box018
FEATURE [Part::Cylinder] Cylinder009
  Angle = 360
  AttacherType = Attacher::AttachEngine3D
  FirstAngle = 0
  Height = 22
  Placement = pos=(98,174,-23) rot=(1,0,0;1.5708rad)
  Radius = 50
  SecondAngle = 0
FEATURE [Part::Cut] Cut023
  Base = -> Box017
  Refine = true
  Tool = -> Cylinder009
FEATURE [Part::Cylinder] Cylinder010
  Angle = 360
  AttacherType = Attacher::AttachEngine3D
  FirstAngle = 0
  Height = 22
  Placement = pos=(98,174,-23) rot=(1,0,0;1.5708rad)
  Radius = 50
  SecondAngle = 0
FEATURE [Part::Cut] Cut025
  Base = -> Box019
  Refine = true
  Tool = -> Cylinder010
FEATURE [Part::Cut] Cut027
  Base = -> Cut023
  Refine = true
  Tool = -> Cut025
FEATURE [Part::Cylinder] Cylinder011
  Angle = 360
  AttacherType = Attacher::AttachEngine3D
  FirstAngle = 0
  Height = 22
  Placement = pos=(98,174,-23) rot=(1,0,0;1.5708rad)
  Radius = 51
  SecondAngle = 0
FEATURE [Part::Cut] Cut026
  Base = -> Box022
  Refine = true
  Tool = -> Cylinder011
FEATURE [Part::Cut] Cut028
  Base = -> Cut027
  Refine = true
  Tool = -> Cut026
FEATURE [Part::Cut] Cut029
  Base = -> Cut028
  Refine = true
  Tool = -> Box021
FEATURE [Part::Cut] Cut031
  Base = -> Cut028
  Refine = true
  Tool = -> Box021
FEATURE [Part::Cylinder] Cylinder012
  Angle = 360
  AttacherType = Attacher::AttachEngine3D
  FirstAngle = 0
  Height = 4
  Placement = pos=(1,48.5,22.5) rot=(0,1,0;1.5708rad)
  Radius = 2.5
  SecondAngle = 0
FEATURE [Part::Cylinder] Cylinder013
  Angle = 360
  AttacherType = Attacher::AttachEngine3D
  FirstAngle = 0
  Height = 3.5
  Placement = pos=(1.5,48.5,22.5) rot=(0,1,0;1.5708rad)
  Radius = 0.9
  SecondAngle = 0
FEATURE [Part::Cut] Cut083
  Base = -> Cylinder012
  Refine = true
  Tool = -> Cylinder013
FEATURE [Part::Cylinder] Cylinder014
  Angle = 360
  AttacherType = Attacher::AttachEngine3D
  FirstAngle = 0
  Height = 3.5
  Placement = pos=(1.5,48.5,22.5) rot=(0,1,0;1.5708rad)
  Radius = 0.9
  SecondAngle = 0
FEATURE [Part::Cylinder] Cylinder015
  Angle = 360
  AttacherType = Attacher::AttachEngine3D
  FirstAngle = 0
  Height = 4
  Placement = pos=(1,48.5,22.5) rot=(0,1,0;1.5708rad)
  Radius = 2.5
  SecondAngle = 0
FEATURE [Part::Cut] Cut084
  Base = -> Cylinder015
  Placement = pos=(0,72,0) rot=(0,0,1;0rad)
  Refine = true
  Tool = -> Cylinder014
FEATURE [Part::Cylinder] Cylinder016
  Angle = 360
  AttacherType = Attacher::AttachEngine3D
  FirstAngle = 0
  Height = 4
  Placement = pos=(1,48.5,22.5) rot=(0,1,0;1.5708rad)
  Radius = 2.75
  SecondAngle = 0
FEATURE [Part::Cylinder] Cylinder017
  Angle = 360
  AttacherType = Attacher::AttachEngine3D
  FirstAngle = 0
  Height = 4
  Placement = pos=(1,120.5,22.5) rot=(0,1,0;1.5708rad)
  Radius = 2.75
  SecondAngle = 0
FEATURE [Part::Cylinder] Cylinder018
  Angle = 360
  AttacherType = Attacher::AttachEngine3D
  FirstAngle = 0
  Height = 22
  Placement = pos=(98,189,-23) rot=(1,0,0;1.5708rad)
  Radius = 50
  SecondAngle = 0
FEATURE [Part::Cylinder] Cylinder019
  Angle = 360
  AttacherType = Attacher::AttachEngine3D
  FirstAngle = 0
  Height = 22
  Placement = pos=(98,189,-23) rot=(1,0,0;1.5708rad)
  Radius = 82
  SecondAngle = 0
FEATURE [Part::Cut] Cut088
  Base = -> Cylinder019
  Placement = pos=(0,-1,0) rot=(0,0,1;0rad)
  Refine = true
  Tool = -> Cylinder018
FEATURE [Part::Cylinder] Cylinder020
  Angle = 360
  AttacherType = Attacher::AttachEngine3D
  FirstAngle = 0
  Height = 22
  Placement = pos=(98,189,-23) rot=(1,0,0;1.5708rad)
  Radius = 82
  SecondAngle = 0
FEATURE [Part::Cylinder] Cylinder021
  Angle = 360
  AttacherType = Attacher::AttachEngine3D
  FirstAngle = 0
  Height = 22
  Placement = pos=(98,189,-23) rot=(1,0,0;1.5708rad)
  Radius = 50
  SecondAngle = 0
FEATURE [Part::Cut] Cut090
  Base = -> Cylinder020
  Placement = pos=(0,-187,0) rot=(0,0,1;0rad)
  Refine = true
  Tool = -> Cylinder021
FEATURE [Part::Cylinder] Cylinder037
  Angle = 360
  AttacherType = Attacher::AttachEngine3D
  FirstAngle = 0
  Height = 15
  Placement = pos=(0,57.5,-17) rot=(0,1,0;1.5708rad)
  Radius = 1.6
  SecondAngle = 0
FEATURE [Part::Cylinder] Cylinder038
  Angle = 360
  AttacherType = Attacher::AttachEngine3D
  FirstAngle = 0
  Height = 15
  Placement = pos=(0,110.5,-17) rot=(0,1,0;1.5708rad)
  Radius = 1.6
  SecondAngle = 0
FEATURE [Part::Cylinder] Cylinder039
  Angle = 360
  AttacherType = Attacher::AttachEngine3D
  FirstAngle = 0
  Height = 2.5
  Placement = pos=(0,57.5,-17) rot=(0,1,0;1.5708rad)
  Radius = 3.2
  SecondAngle = 0
FEATURE [Part::Cylinder] Cylinder040
  Angle = 360
  AttacherType = Attacher::AttachEngine3D
  FirstAngle = 0
  Height = 2.5
  Placement = pos=(0,110.5,-17) rot=(0,1,0;1.5708rad)
  Radius = 3.2
  SecondAngle = 0
FEATURE [Part::Cylinder] Cylinder041
  Angle = 360
  AttacherType = Attacher::AttachEngine3D
  FirstAngle = 0
  Height = 2.5
  Placement = pos=(0,57.5,-17) rot=(0,1,0;1.5708rad)
  Radius = 5
  SecondAngle = 0
FEATURE [Part::Cylinder] Cylinder042
  Angle = 360
  AttacherType = Attacher::AttachEngine3D
  FirstAngle = 0
  Height = 2.5
  Placement = pos=(0,110.5,-17) rot=(0,1,0;1.5708rad)
  Radius = 5
  SecondAngle = 0
FEATURE [Part::Cylinder] Cylinder043
  Angle = 65
  AttacherType = Attacher::AttachEngine3D
  FirstAngle = 0
  Height = 18
  Placement = pos=(98,153,-23) rot=(0.992433,0.086827,-0.086827;1.57839rad)
  Radius = 50
  SecondAngle = 0
FEATURE [Part::Cylinder] Cylinder044
  Angle = 360
  AttacherType = Attacher::AttachEngine3D
  FirstAngle = 0
  Height = 18
  Placement = pos=(98,153,-23) rot=(1,0,0;1.5708rad)
  Radius = 48
  SecondAngle = 0
FEATURE [Part::Cut] Cut107
  Base = -> Cylinder043
  Refine = true
  Tool = -> Cylinder044
FEATURE [Part::Cylinder] Cylinder045
  Angle = 360
  AttacherType = Attacher::AttachEngine3D
  FirstAngle = 0
  Height = 18
  Placement = pos=(98,153,-23) rot=(1,0,0;1.5708rad)
  Radius = 48
  SecondAngle = 0
FEATURE [Part::Cylinder] Cylinder046
  Angle = 65
  AttacherType = Attacher::AttachEngine3D
  FirstAngle = 0
  Height = 18
  Placement = pos=(98,153,-23) rot=(0.992433,0.086827,-0.086827;1.57839rad)
  Radius = 50
  SecondAngle = 0
FEATURE [Part::Cut] Cut108
  Base = -> Cylinder046
  Placement = pos=(0,-120,0) rot=(0,0,1;0rad)
  Refine = true
  Tool = -> Cylinder045
FEATURE [Part::Cylinder] Cylinder047
  Angle = 65
  AttacherType = Attacher::AttachEngine3D
  FirstAngle = 0
  Height = 0.5
  Placement = pos=(98,153,-23) rot=(0.992433,0.086827,-0.086827;1.57839rad)
  Radius = 50
  SecondAngle = 0
FEATURE [Part::Cylinder] Cylinder048
  Angle = 360
  AttacherType = Attacher::AttachEngine3D
  FirstAngle = 0
  Height = 0.5
  Placement = pos=(98,153,-23) rot=(1,0,0;1.5708rad)
  Radius = 49.5
  SecondAngle = 0
FEATURE [Part::Cut] Cut111
  Base = -> Cylinder047
  Placement = pos=(0,-151,0) rot=(0,0,1;0rad)
  Refine = true
  Tool = -> Cylinder048
FEATURE [Part::Cylinder] Cylinder049
  Angle = 65
  AttacherType = Attacher::AttachEngine3D
  FirstAngle = 0
  Height = 0.5
  Placement = pos=(98,153,-23) rot=(0.992433,0.086827,-0.086827;1.57839rad)
  Radius = 50
  SecondAngle = 0
FEATURE [Part::Cylinder] Cylinder050
  Angle = 360
  AttacherType = Attacher::AttachEngine3D
  FirstAngle = 0
  Height = 0.5
  Placement = pos=(98,153,-23) rot=(1,0,0;1.5708rad)
  Radius = 49.5
  SecondAngle = 0
FEATURE [Part::Cut] Cut112
  Base = -> Cylinder049
  Placement = pos=(0,13,0) rot=(0,0,1;0rad)
  Refine = true
  Tool = -> Cylinder050
FEATURE [Part::Cylinder] Cylinder051
  Angle = 360
  AttacherType = Attacher::AttachEngine3D
  FirstAngle = 0
  Height = 87
  Placement = pos=(154,47,29) rot=(0,0,1;0rad)
  Radius = 4.5
  SecondAngle = 0
FEATURE [Part::Cylinder] Cylinder052
  Angle = 360
  AttacherType = Attacher::AttachEngine3D
  FirstAngle = 0
  Height = 80
  Placement = pos=(154,48,38) rot=(0,0,1;0rad)
  Radius = 4.6
  SecondAngle = 0
FEATURE [Part::Cylinder] Cylinder053
  Angle = 360
  AttacherType = Attacher::AttachEngine3D
  FirstAngle = 0
  Height = 10
  Placement = pos=(150,39.5,41) rot=(0,1,0;1.5708rad)
  Radius = 1.1
  SecondAngle = 0
FEATURE [Part::Cylinder] Cylinder054
  Angle = 360
  AttacherType = Attacher::AttachEngine3D
  FirstAngle = 0
  Height = 10
  Placement = pos=(150,54.5,41) rot=(0,1,0;1.5708rad)
  Radius = 1.1
  SecondAngle = 0
FEATURE [Part::Cylinder] Cylinder055
  Angle = 360
  AttacherType = Attacher::AttachEngine3D
  FirstAngle = 0
  Height = 6
  Placement = pos=(154,47,38) rot=(0,0,1;0rad)
  Radius = 5.5
  SecondAngle = 0
FEATURE [Part::Cylinder] Cylinder056
  Angle = 360
  AttacherType = Attacher::AttachEngine3D
  FirstAngle = 0
  Height = 10
  Placement = pos=(146,47,107) rot=(0,1,0;1.5708rad)
  Radius = 0.9
  SecondAngle = 0
FEATURE [Part::Cylinder] Cylinder057
  Angle = 360
  AttacherType = Attacher::AttachEngine3D
  FirstAngle = 0
  Height = 10
  Placement = pos=(144,47,107) rot=(0,1,0;1.5708rad)
  Radius = 1.1
  SecondAngle = 0
FEATURE [Part::Cut] Cut118  label="snorkel-support"
  Base = -> Box212
  Refine = true
  Tool = -> Cylinder057
FEATURE [Part::Cylinder] Cylinder058
  Angle = 360
  AttacherType = Attacher::AttachEngine3D
  FirstAngle = 0
  Height = 5
  Placement = pos=(154,47,32) rot=(0,0,1;0rad)
  Radius = 2
  SecondAngle = 0
FEATURE [Part::Cylinder] Cylinder059
  Angle = 360
  AttacherType = Attacher::AttachEngine3D
  FirstAngle = 0
  Height = 3
  Placement = pos=(6,140.5,-16.5) rot=(0,1,0;1.5708rad)
  Radius = 4
  SecondAngle = 0
FEATURE [Part::Cylinder] Cylinder060
  Angle = 360
  AttacherType = Attacher::AttachEngine3D
  FirstAngle = 0
  Height = 3
  Placement = pos=(6,140.5,-16.5) rot=(0,1,0;1.5708rad)
  Radius = 2.5
  SecondAngle = 0
FEATURE [Part::Cylinder] Cylinder061
  Angle = 360
  AttacherType = Attacher::AttachEngine3D
  FirstAngle = 0
  Height = 3
  Placement = pos=(6,140.5,-16.5) rot=(0,1,0;1.5708rad)
  Radius = 4
  SecondAngle = 0
FEATURE [Part::Cylinder] Cylinder064
  Angle = 360
  AttacherType = Attacher::AttachEngine3D
  FirstAngle = 0
  Height = 3
  Placement = pos=(154,54,25.65) rot=(1,0,0;1.0472rad)
  Radius = 4.5
  SecondAngle = 0
FEATURE [Part::Cylinder] Cylinder065
  Angle = 360
  AttacherType = Attacher::AttachEngine3D
  FirstAngle = 0
  Height = 5
  Placement = pos=(154,47,32) rot=(0,0,1;0rad)
  Radius = 2.1
  SecondAngle = 0
FEATURE [Part::Cylinder] Cylinder066
  Angle = 360
  AttacherType = Attacher::AttachEngine3D
  FirstAngle = 0
  Height = 10
  Placement = pos=(0,140,-16.5) rot=(0,1,0;1.5708rad)
  Radius = 2.5
  SecondAngle = 0
FEATURE [Part::Cylinder] Cylinder067
  Angle = 360
  AttacherType = Attacher::AttachEngine3D
  FirstAngle = 0
  Height = 3
  Placement = pos=(6,140.5,-16.5) rot=(0,1,0;1.5708rad)
  Radius = 2.5
  SecondAngle = 0
FEATURE [Part::Fillet] Fillet013
  Base = -> Box013
  Edges = 2 edges r=20: [Edge1,Edge3]
FEATURE [Part::Fillet] Fillet014
  Base = -> Box014
  Edges = 2 edges r=20: [Edge1,Edge3]
FEATURE [Part::Fillet] Fillet015
  Base = -> Fillet013
  Edges = 2 edges r=10: [Edge17,Edge18]
FEATURE [Part::Fillet] Fillet016
  Base = -> Box015
  Edges = 2 edges r=18: [Edge1,Edge3]
FEATURE [Part::Cut] Cut018
  Base = -> Fillet014
  Refine = true
  Tool = -> Fillet016
FEATURE [Part::Fillet] Fillet017
  Base = -> Box016
  Edges = 2 edges r=16: [Edge1,Edge3]
FEATURE [Part::Fillet] Fillet018
  Base = -> Fillet017
  Edges = 2 edges r=6: [Edge17,Edge18]
FEATURE [Part::Cut] Cut019
  Base = -> Fillet015
  Refine = true
  Tool = -> Fillet018
FEATURE [Part::Cut] Cut020
  Base = -> Cut019
  Refine = true
  Tool = -> Cylinder005
FEATURE [Part::Cut] Cut003
  Base = -> Cut020
  Refine = true
  Tool = -> Cut018
FEATURE [Part::Fillet] Fillet030
  Base = -> Box020
  Edges = 2 edges r=14: [Edge1,Edge3]
FEATURE [Part::Fillet] Fillet031
  Base = -> Box023
  Edges = 2 edges r=10: [Edge1,Edge3]
FEATURE [Part::Cut] Cut030
  Base = -> Fillet030
  Refine = true
  Tool = -> Fillet031
FEATURE [Part::Fillet] Fillet032
  Base = -> Box024
  Edges = 2 edges r=16: [Edge1,Edge3]
  Placement = pos=(0,0,-9) rot=(0,0,1;0rad)
FEATURE [Part::Fillet] Fillet033
  Base = -> Fillet032
  Edges = 2 edges r=7: [Edge17,Edge18]
  Placement = pos=(0,0,9) rot=(0,0,1;0rad)
FEATURE [Part::Fillet] Fillet034
  Base = -> Box025
  Edges = 4 edges r=5: [Edge9,Edge10,Edge11,Edge12]
  Placement = pos=(44,0,0) rot=(0,0,1;0rad)
FEATURE [Part::Fillet] Fillet038  label="bumper_00"
  Base = -> Cut030
  Edges = 2 edges r=2: [Edge1,Edge4]
FEATURE [Part::Fillet] Fillet043
  Base = -> Box026
  Edges = 2 edges r=16: [Edge1,Edge3]
FEATURE [Part::Fillet] Fillet044
  Base = -> Fillet043
  Edges = 2 edges r=7: [Edge17,Edge18]
FEATURE [Part::Fillet] Fillet045
  Base = -> Fillet044
  Edges = 1 edges r=6.99: [Edge5]
FEATURE [Part::Fillet] Fillet055
  Base = -> Box035
  Edges = 4 edges r=4: [Edge9,Edge10,Edge11,Edge12]
  Placement = pos=(11,0,0) rot=(0,0,1;0rad)
FEATURE [Part::Cut] Cut033
  Base = -> Fillet034
  Refine = true
  Tool = -> Fillet055
FEATURE [Part::Fillet] Fillet083
  Base = -> Box085
  Edges = 4 edges r=3: [Edge1,Edge3,Edge5,Edge7]
FEATURE [Part::Fillet] Fillet087
  Base = -> Box092
  Edges = 4 edges r=3: [Edge9,Edge10,Edge11,Edge12]
  Placement = pos=(0,3,0) rot=(0,0,1;0rad)
FEATURE [Part::Fillet] Fillet088
  Base = -> Box093
  Edges = 4 edges r=3: [Edge9,Edge10,Edge11,Edge12]
  Placement = pos=(0,116,0) rot=(0,0,1;0rad)
FEATURE [Part::Fillet] Fillet097
  Base = -> Box114
  Edges = 4 edges r=4: [Edge9,Edge10,Edge11,Edge12]
  Placement = pos=(11,0,0) rot=(0,0,1;0rad)
FEATURE [Part::Cut] Cut079
  Base = -> Box115
  Refine = true
  Tool = -> Fillet097
FEATURE [Part::Fillet] Fillet103
  Base = -> Box202
  Edges = 2 edges r=13: [Edge1,Edge3]
FEATURE [Part::Fillet] Fillet104
  Base = -> Fillet103
  Edges = 2 edges r=3: [Edge17,Edge18]
FEATURE [Part::Fillet] Fillet105
  Base = -> Box203
  Edges = 2 edges r=2.5: [Edge5,Edge7]
FEATURE [Part::Fillet] Fillet106
  Base = -> Fillet105
  Edges = 2 edges r=12.5: [Edge17,Edge18]
FEATURE [Part::Fillet] Fillet107
  Base = -> Fillet015
  Edges = 1 edges r=2: [Edge31]
  Placement = pos=(-6,0,0) rot=(0,0,1;0rad)
FEATURE [Part::Fillet] Fillet108
  Base = -> Cut003
  Edges = 2 edges r=3: [Edge4,Edge16]
FEATURE [Part::Fillet] Fillet109
  Base = -> Box206
  Edges = 4 edges r=3: [Edge1,Edge3,Edge5,Edge7]
FEATURE [Part::Fillet] Fillet111
  Base = -> Box207
  Edges = 4 edges r=4: [Edge1,Edge3,Edge5,Edge7]
FEATURE [Part::Fillet] Fillet112
  Base = -> Fillet109
  Edges = 4 edges r=2: [Edge1,Edge7,Edge8,Edge11]
FEATURE [Part::Fillet] Fillet131
  Base = -> Box251
  Edges = 4 edges r=3: [Edge9,Edge10,Edge11,Edge12]
  Placement = pos=(2,116,0) rot=(0,0,1;0rad)
FEATURE [Part::Fillet] Fillet132
  Base = -> Box252
  Edges = 4 edges r=3: [Edge9,Edge10,Edge11,Edge12]
  Placement = pos=(0,116,0) rot=(0,0,1;0rad)
FEATURE [Part::Fillet] Fillet133  label="front-lights-glass"
  Base = -> Fillet132
  Edges = 4 edges r=0.4: [Edge1,Edge4,Edge5,Edge8]
  Placement = pos=(1,0.5,0) rot=(0,0,1;0rad)
FEATURE [Part::Fillet] Fillet136
  Base = -> Box258
  Edges = 4 edges r=2: [Edge9,Edge10,Edge11,Edge12]
FEATURE [Part::Fillet] Fillet137
  Base = -> Box259
  Edges = 4 edges r=2: [Edge9,Edge10,Edge11,Edge12]
FEATURE [Part::MultiFuse] Fusion010
  Refine = true
  Shapes = -> [Cut029,Cut024]
FEATURE [Part::MultiFuse] Fusion011  label="right-wing_00"
  Placement = pos=(0,1,0) rot=(0,0,1;0rad)
  Refine = true
  Shapes = -> [Cut031,Cut032]
FEATURE [Part::Cut] Cut089
  Base = -> Fusion011
  Refine = true
  Tool = -> Cut088
FEATURE [Part::Fillet] Fillet099
  Base = -> Cut089
  Edges = 1 edges r=2: [Edge58]
FEATURE [Part::MultiFuse] Fusion012
  Placement = pos=(0.5,36,0) rot=(0,0,1;0rad)
  Refine = true
  Shapes = -> [Box038,Box039]
FEATURE [Part::MultiFuse] Fusion013
  Placement = pos=(0.5,0,0) rot=(0,0,1;0rad)
  Refine = true
  Shapes = -> [Box041,Box040]
FEATURE [Part::Cut] Cut105  label="cab_tilt_lower"
  Base = -> Fusion013
  Refine = true
  Tool = -> Fusion012
FEATURE [Part::MultiFuse] Fusion014
  Placement = pos=(0.5,-36,0) rot=(0,0,1;0rad)
  Refine = true
  Shapes = -> [Box043,Box042]
FEATURE [Part::MultiFuse] Fusion017  label="roof_00"
  Refine = true
  Shapes = -> [Fillet033,Fillet045]
FEATURE [Part::Cut] Cut062
  Base = -> Fusion017
  Refine = true
  Tool = -> Fillet083
FEATURE [Part::Fillet] Fillet084  label="roof_001"
  Base = -> Cut062
  Edges = 1 edges r=0.99: [Edge56]
FEATURE [Part::MultiFuse] Fusion041
  Refine = true
  Shapes = -> [Fillet088,Fillet087]
FEATURE [Part::Cut] Cut066
  Base = -> Fillet038
  Refine = true
  Tool = -> Fusion041
FEATURE [Part::Fillet] Fillet090
  Base = -> Cut066
  Edges = 1 edges r=1.2: [Edge7]
FEATURE [Part::Fillet] Fillet091  label="bumper_001"
  Base = -> Fillet090
  Edges = 1 edges r=1.2: [Edge17]
  Placement = pos=(0,0,-0.5) rot=(0,0,1;0rad)
FEATURE [Part::MultiFuse] Fusion049
  Refine = true
  Shapes = -> [Box046,Box044,Box045]
FEATURE [Part::MultiFuse] Fusion051
  Refine = true
  Shapes = -> [Box122,Box123,Box124,Box125,Box126,Box127,Box128,Box129,Box130,Box131,Box132,Box133,Box134,Box135,Box136]
FEATURE [Part::MultiFuse] Fusion052
  Placement = pos=(0,0,14) rot=(0,0,1;0rad)
  Refine = true
  Shapes = -> [Box142,Box150,Box144,Box138,Box140,Box146,Box145,Box141,Box151,Box147,Box139,Box137,Box149,Box143,Box148]
FEATURE [Part::MultiFuse] Fusion053
  Refine = true
  Shapes = -> [Fusion052,Fusion051]
FEATURE [Part::MultiFuse] Fusion054
  Placement = pos=(0,15.5,0) rot=(0,0,1;0rad)
  Refine = true
  Shapes = -> [Box116,Box118,Box121,Box119,Fusion053,Box117,Box120]
FEATURE [Part::MultiFuse] Fusion056
  Refine = true
  Shapes = -> [Fusion052,Fusion051]
FEATURE [Part::MultiFuse] Fusion055
  Placement = pos=(0,-4.5,0) rot=(0,0,1;0rad)
  Refine = true
  Shapes = -> [Box154,Box156,Box157,Box155,Fusion056,Box152,Box153]
FEATURE [Part::MultiFuse] Fusion058
  Refine = true
  Shapes = -> [Fusion052,Fusion051]
FEATURE [Part::MultiFuse] Fusion057
  Placement = pos=(0,35.5,0) rot=(0,0,1;0rad)
  Refine = true
  Shapes = -> [Box160,Box162,Box163,Box161,Fusion058,Box158,Box159]
FEATURE [Part::MultiFuse] Fusion060
  Refine = true
  Shapes = -> [Fusion052,Fusion051]
FEATURE [Part::MultiFuse] Fusion059
  Placement = pos=(0,55.5,0) rot=(0,0,1;0rad)
  Refine = true
  Shapes = -> [Box168,Box166,Box164,Box169,Fusion060,Box165,Box167]
FEATURE [Part::MultiFuse] Fusion062
  Refine = true
  Shapes = -> [Fusion052,Fusion051]
FEATURE [Part::MultiFuse] Fusion061
  Placement = pos=(0,75.5,0) rot=(0,0,1;0rad)
  Refine = true
  Shapes = -> [Box174,Box175,Box173,Box172,Fusion062,Box170,Box171]
FEATURE [Part::MultiFuse] Fusion063
  Refine = true
  Shapes = -> [Fusion052,Fusion051]
FEATURE [Part::MultiFuse] Fusion064
  Placement = pos=(0,95.5,0) rot=(0,0,1;0rad)
  Refine = true
  Shapes = -> [Box180,Box181,Box179,Box176,Fusion063,Box178,Box177]
FEATURE [Part::MultiFuse] Fusion065
  Refine = true
  Shapes = -> [Fusion052,Fusion051]
FEATURE [Part::MultiFuse] Fusion066
  Placement = pos=(0,99.5,0) rot=(0,0,1;0rad)
  Refine = true
  Shapes = -> [Box184,Box187,Box183,Box186,Fusion065,Box185,Box182]
FEATURE [Part::MultiFuse] Fusion067
  Refine = true
  Shapes = -> [Fusion054,Fusion057,Fusion055,Fusion059,Fusion064,Fusion061,Fusion066]
FEATURE [Part::Cut] Cut082
  Base = -> Fusion067
  Refine = true
  Tool = -> Cut079
FEATURE [Part::MultiFuse] Fusion069
  Refine = true
  Shapes = -> [Cylinder016,Cylinder017]
FEATURE [Part::Cut] Cut085  label="radiator-grid"
  Base = -> Cut082
  Refine = true
  Tool = -> Fusion069
FEATURE [Part::MultiFuse] Fusion070
  Refine = true
  Shapes = -> [Box055,Box056]
FEATURE [Part::Cut] Cut087
  Base = -> Cut033
  Refine = true
  Tool = -> Fusion070
FEATURE [Part::MultiFuse] Fusion071
  Refine = true
  Shapes = -> [Box036,Box037]
FEATURE [Part::MultiFuse] Fusion072
  Placement = pos=(-0.5,0,0) rot=(0,0,1;0rad)
  Refine = true
  Shapes = -> [Fusion012,Fusion013,Fusion014,Fusion071]
FEATURE [Part::Cut] Cut086
  Base = -> Fusion072
  Refine = true
  Tool = -> Fusion049
FEATURE [Part::MultiFuse] Fusion073
  Placement = pos=(-0.5,0,0) rot=(0,0,1;0rad)
  Refine = true
  Shapes = -> [Cut084,Cut083]
FEATURE [Part::MultiFuse] Fusion074  label="radiator-mask"
  Refine = true
  Shapes = -> [Cut087,Fusion073,Cut086]
FEATURE [Part::MultiFuse] Fusion079
  Refine = true
  Shapes = -> [Box192,Fillet099]
FEATURE [Part::Fillet] Fillet102  label="right-wing_01"
  Base = -> Fusion079
  Edges = 1 edges r=2: [Edge72]
FEATURE [Part::MultiFuse] Fusion092
  Refine = true
  Shapes = -> [Cylinder037,Cylinder038]
FEATURE [Part::MultiFuse] Fusion093
  Placement = pos=(-2,0,0) rot=(0,0,1;0rad)
  Refine = true
  Shapes = -> [Cylinder039,Cylinder040,Fusion092]
FEATURE [Part::MultiFuse] Fusion094
  Placement = pos=(6,0,0) rot=(0,0,1;0rad)
  Refine = true
  Shapes = -> [Cylinder041,Cylinder042]
FEATURE [Part::MultiFuse] Fusion095
  Refine = true
  Shapes = -> [Fusion094,Fillet091]
FEATURE [Part::Cut] Cut103  label="bumper"
  Base = -> Fusion095
  Refine = true
  Tool = -> Fusion093
FEATURE [Part::MultiFuse] Fusion096
  Refine = true
  Shapes = -> [Fillet084,Fillet104]
FEATURE [Part::Cut] Cut104  label="roof"
  Base = -> Fusion096
  Refine = true
  Tool = -> Fillet106
FEATURE [Part::MultiFuse] Fusion098  label="axles"
  Refine = true
  Shapes = -> [Fillet017,Cylinder017,Cylinder019,Cylinder018]
FEATURE [Part::MultiFuse] Fusion101
  Refine = true
  Shapes = -> [Cut107,Fillet102]
FEATURE [Part::Cut] Cut110
  Base = -> Fusion101
  Placement = pos=(0,2,0) rot=(0,0,1;0rad)
  Refine = true
  Tool = -> Box205
FEATURE [Part::Cut] Cut114  label="right-wing"
  Base = -> Cut110
  Placement = pos=(0,-1,0) rot=(0,0,1;0rad)
  Refine = true
  Tool = -> Cut112
FEATURE [Part::MultiFuse] Fusion103
  Refine = true
  Shapes = -> [Fillet112,Fillet111]
FEATURE [Part::Cut] Cut115  label="snorkel-cap"
  Base = -> Fusion103
  Placement = pos=(0,-1,0) rot=(0,0,1;0rad)
  Refine = true
  Tool = -> Cylinder052
FEATURE [Part::MultiFuse] Fusion104
  Refine = true
  Shapes = -> [Cylinder053,Cylinder054]
FEATURE [Part::MultiFuse] Fusion105
  Refine = true
  Shapes = -> [Cylinder055,Box211]
FEATURE [Part::Cut] Cut116
  Base = -> Fusion105
  Refine = true
  Tool = -> Box210
FEATURE [Part::Cut] Cut117
  Base = -> Cut116
  Placement = pos=(-0.5,0,0) rot=(0,0,1;0rad)
  Refine = true
  Tool = -> Fusion104
FEATURE [Part::MultiFuse] Fusion106
  Refine = true
  Shapes = -> [Box219,Box220]
FEATURE [Part::Cut] Cut129
  Base = -> Box218
  Placement = pos=(0.5,0,0) rot=(0,0,1;0rad)
  Refine = true
  Tool = -> Fusion106
FEATURE [Part::MultiFuse] Fusion107
  Refine = true
  Shapes = -> [Box222,Box223]
FEATURE [Part::Cut] Cut120
  Base = -> Box221
  Refine = true
  Tool = -> Fusion107
FEATURE [Part::MultiFuse] Fusion108
  Refine = true
  Shapes = -> [Box225,Box226]
FEATURE [Part::Cut] Cut121
  Base = -> Box224
  Placement = pos=(0.5,0,0) rot=(0,0,1;0rad)
  Refine = true
  Tool = -> Fusion108
FEATURE [Part::Cut] Cut119
  Base = -> Cut120
  Placement = pos=(0,0,0.5) rot=(0,0,1;0rad)
  Refine = true
  Tool = -> Cut121
FEATURE [Part::MultiFuse] Fusion109
  Refine = true
  Shapes = -> [Box213,Cylinder051,Cut117]
FEATURE [Part::MultiFuse] Fusion110
  Refine = true
  Shapes = -> [Cylinder058,Fusion109]
FEATURE [Part::Cut] Cut123  label="snorkel-pipe"
  Base = -> Fusion110
  Refine = true
  Tool = -> Cylinder056
FEATURE [Part::MultiFuse] Fusion111
  Refine = true
  Shapes = -> [Box234,Box235]
FEATURE [Part::Cut] Cut132
  Base = -> Box233
  Refine = true
  Tool = -> Fusion111
FEATURE [Part::MultiFuse] Fusion115
  Refine = true
  Shapes = -> [Box215,Box208]
FEATURE [Part::Cut] Cut126
  Base = -> Box214
  Refine = true
  Tool = -> Fusion115
FEATURE [Part::MultiFuse] Fusion116
  Refine = true
  Shapes = -> [Box216,Box217]
FEATURE [Part::Cut] Cut128
  Base = -> Box209
  Refine = true
  Tool = -> Fusion116
FEATURE [Part::Cut] Cut127
  Base = -> Cut128
  Placement = pos=(8,0,0.5) rot=(0,0,1;0rad)
  Refine = true
  Tool = -> Cut129
FEATURE [Part::MultiFuse] Fusion117
  Refine = true
  Shapes = -> [Box228,Box229]
FEATURE [Part::Cut] Cut130
  Base = -> Box227
  Refine = true
  Tool = -> Fusion117
FEATURE [Part::MultiFuse] Fusion118
  Refine = true
  Shapes = -> [Box231,Box232]
FEATURE [Part::Cut] Cut124
  Base = -> Box230
  Placement = pos=(0.5,0,0) rot=(0,0,1;0rad)
  Refine = true
  Tool = -> Fusion118
FEATURE [Part::Cut] Cut122
  Base = -> Cut130
  Placement = pos=(16,0,0.5) rot=(0,0,1;0rad)
  Refine = true
  Tool = -> Cut124
FEATURE [Part::MultiFuse] Fusion119
  Refine = true
  Shapes = -> [Box237,Box238]
FEATURE [Part::Cut] Cut133
  Base = -> Box236
  Placement = pos=(0.5,0,0) rot=(0,0,1;0rad)
  Refine = true
  Tool = -> Fusion119
FEATURE [Part::Cut] Cut131
  Base = -> Cut132
  Placement = pos=(32,0,0.5) rot=(0,0,1;0rad)
  Refine = true
  Tool = -> Cut133
FEATURE [Part::MultiFuse] Fusion120
  Refine = true
  Shapes = -> [Box240,Box241]
FEATURE [Part::Cut] Cut135
  Base = -> Box239
  Refine = true
  Tool = -> Fusion120
FEATURE [Part::MultiFuse] Fusion121
  Refine = true
  Shapes = -> [Box243,Box244]
FEATURE [Part::Cut] Cut136
  Base = -> Box242
  Placement = pos=(0.5,0,0) rot=(0,0,1;0rad)
  Refine = true
  Tool = -> Fusion121
FEATURE [Part::Cut] Cut134
  Base = -> Cut135
  Placement = pos=(24,0,0.5) rot=(0,0,1;0rad)
  Refine = true
  Tool = -> Cut136
FEATURE [Part::MultiFuse] Fusion114
  Refine = true
  Shapes = -> [Cut126,Cut127,Cut119,Cut122,Cut131,Cut134,Box245,Box246]
FEATURE [Part::MultiFuse] Fusion123
  Refine = true
  Shapes = -> [Box248,Box249]
FEATURE [Part::Cut] Cut137
  Base = -> Box247
  Refine = true
  Tool = -> Fusion123
FEATURE [Part::MultiFuse] Fusion125
  Refine = true
  Shapes = -> [Fillet136,Cylinder059]
FEATURE [Part::Cut] Cut140  label="front-lights-right-proyector-holder"
  Base = -> Fusion125
  Refine = true
  Tool = -> Cylinder067
FEATURE [Part::MultiFuse] Fusion126
  Refine = true
  Shapes = -> [Fillet137,Cylinder061]
FEATURE [Part::Cut] Cut141
  Base = -> Fusion126
  Refine = true
  Tool = -> Cylinder060
FEATURE [Part::Mirroring] Part__Mirroring002  label="left-wing_00"
  Base = (0,0,0)
  Normal = (0,1,0)
  Placement = pos=(0,167,0) rot=(0,0,1;0rad)
  Source = -> Fusion010
FEATURE [Part::Cut] Cut091
  Base = -> Part__Mirroring002
  Refine = true
  Tool = -> Cut090
FEATURE [Part::Fillet] Fillet098
  Base = -> Cut091
  Edges = 1 edges r=2: [Edge58]
FEATURE [Part::Fillet] Fillet101
  Base = -> Fillet098
  Edges = 1 edges r=2: [Edge37]
FEATURE [Part::MultiFuse] Fusion078  label="left-wing_01"
  Refine = true
  Shapes = -> [Fillet101,Box188]
FEATURE [Part::MultiFuse] Fusion099  label="frame-bars"
  Refine = true
  Shapes = -> [Cut019,Part__Mirroring002]
FEATURE [Part::MultiFuse] Fusion097  label="frame"
  Placement = pos=(13,44,-15) rot=(0,0,1;0rad)
  Refine = true
  Shapes = -> [Cut106,Fillet107,Fusion099,Fillet108,Cut105,Fusion098]
FEATURE [Part::MultiFuse] Fusion100
  Refine = true
  Shapes = -> [Fusion078,Cut108]
FEATURE [Part::Cut] Cut109
  Base = -> Fusion100
  Placement = pos=(0,-2,0) rot=(0,0,1;0rad)
  Refine = true
  Tool = -> Box204
FEATURE [Part::Cut] Cut113  label="left-wing"
  Base = -> Cut109
  Placement = pos=(0,1,0) rot=(0,0,1;0rad)
  Refine = true
  Tool = -> Cut111
FEATURE [Part::Mirroring] Part__Mirroring016  label="front-lights-left-proyector-holder"
  Base = (0,0,0)
  Normal = (0,1,0)
  Placement = pos=(0,168,0) rot=(0,0,1;0rad)
  Source = -> Cut141
FEATURE [Part::Part2DObjectPython] ShapeString  # Draft 2D object (typed FeaturePython)
  FontFile = <path>
  MapMode = 5
  Placement = pos=(0.2,0.6,1) rot=(0,0,1;0rad)
  Size = 6
  String = F
  Tracking = 0
FEATURE [Part::Extrusion] Extrude003
  Base = -> ShapeString
  Dir = (0,0,0.5)
  DirMode = 0
  FaceMakerClass = Part::FaceMakerExtrusion
  LengthFwd = 0
  LengthRev = 0
  Placement = pos=(2,0.5,-0.5) rot=(0,0,1;0rad)
  Solid = false
  Symmetric = false
FEATURE [Part::Part2DObjectPython] ShapeString001  # Draft 2D object (typed FeaturePython)
  FontFile = <path>
  MapMode = 5
  Placement = pos=(18.2,0.6,1) rot=(0,0,1;0rad)
  Size = 6
  String = A
  Tracking = 0
FEATURE [Part::Extrusion] Extrude004
  Base = -> ShapeString001
  Dir = (0,0,0.5)
  DirMode = 0
  FaceMakerClass = Part::FaceMakerExtrusion
  LengthFwd = 0
  LengthRev = 0
  Placement = pos=(0,0.5,-0.5) rot=(0,0,1;0rad)
  Solid = false
  Symmetric = false
FEATURE [Part::Part2DObjectPython] ShapeString002  # Draft 2D object (typed FeaturePython)
  FontFile = <path>
  MapMode = 5
  Placement = pos=(26.5,0.6,1) rot=(0,0,1;0rad)
  Size = 6
  String = T
  Tracking = 0
FEATURE [Part::Extrusion] Extrude005
  Base = -> ShapeString002
  Dir = (0,0,0.5)
  DirMode = 0
  FaceMakerClass = Part::FaceMakerExtrusion
  LengthFwd = 0
  LengthRev = 0
  Placement = pos=(0,0.5,-0.5) rot=(0,0,1;0rad)
  Solid = false
  Symmetric = false
FEATURE [Part::Part2DObjectPython] ShapeString003  # Draft 2D object (typed FeaturePython)
  FontFile = <path>
  MapMode = 5
  Placement = pos=(12,0.6,1) rot=(0,0,1;0rad)
  Size = 6
  String = I
  Tracking = 0
FEATURE [Part::Extrusion] Extrude006
  Base = -> ShapeString003
  Dir = (0,0,0.5)
  DirMode = 0
  FaceMakerClass = Part::FaceMakerExtrusion
  LengthFwd = 0
  LengthRev = 0
  Placement = pos=(0,0.5,-0.5) rot=(0,0,1;0rad)
  Solid = false
  Symmetric = false
FEATURE [Part::MultiFuse] Fusion102  label="cab-fiat-logo"
  Placement = pos=(0,102,43) rot=(0.57735,-0.57735,-0.57735;2.0944rad)
  Refine = true
  Shapes = -> [Extrude003,Extrude004,Extrude005,Fusion114,Extrude006]
FEATURE [Part::Part2DObjectPython] ShapeString004  # Draft 2D object (typed FeaturePython)
  FontFile = <path>
  MapMode = 5
  Placement = pos=(1,0.3,1) rot=(0,0,1;0rad)
  Size = 4.5
  String = 180
  Tracking = 0
FEATURE [Part::Extrusion] Extrude007
  Base = -> ShapeString004
  Dir = (0,0,0.5)
  DirMode = 0
  FaceMakerClass = Part::FaceMakerExtrusion
  LengthFwd = 0
  LengthRev = 0
  Solid = false
  Symmetric = false
FEATURE [Part::MultiFuse] Fusion122  label="cab-180-logo"
  Placement = pos=(2,40,12) rot=(0.57735,-0.57735,-0.57735;2.0944rad)
  Refine = true
  Shapes = -> [Extrude007,Cut137]
FEATURE [Part::Feature] Solid006
  Placement = pos=(-0.31,0,0) rot=(0,0,1;0rad)
  shape: bbox 5.543 x 22 x 15.99 mm, 10 faces (baked)
FEATURE [Part::Cut] Cut138
  Base = -> Fillet131
  Refine = true
  Tool = -> Solid006
FEATURE [Part::Cut] Cut139  label="front-lights-right-proyector"
  Base = -> Cut138
  Placement = pos=(1,0.5,0) rot=(0,0,1;0rad)
  Refine = true
  Tool = -> Cylinder066
FEATURE [Part::Torus] Torus002
  Angle1 = -180
  Angle2 = 180
  Angle3 = 60
  AttacherType = Attacher::AttachEngine3D
  Placement = pos=(0,0,0) rot=(0,1,0;1.5708rad)
  Radius1 = 10
  Radius2 = 4.5
FEATURE [Part::Mirroring] Part__Mirroring017  label="Torus (Mirror #17)001"
  Base = (0,0,0)
  Normal = (0,1,0)
  Placement = pos=(154,57,36) rot=(-1,0,0;0.523599rad)
  Source = -> Torus002
FEATURE [Part::Torus] Torus003
  Angle1 = -180
  Angle2 = 180
  Angle3 = 60
  AttacherType = Attacher::AttachEngine3D
  Placement = pos=(154,49,17) rot=(0.57735,0.57735,0.57735;2.0944rad)
  Radius1 = 10
  Radius2 = 4.5
FEATURE [Part::MultiFuse] Fusion112
  Placement = pos=(0,0.6,0.2) rot=(0,0,1;0rad)
  Refine = true
  Shapes = -> [Cylinder064,Torus003]
FEATURE [Part::MultiFuse] Fusion113
  Refine = true
  Shapes = -> [Part__Mirroring017,Fusion112]
FEATURE [Part::Cut] Cut125  label="snorkel-s-pipe"
  Base = -> Fusion113
  Placement = pos=(0,0,-7) rot=(0,0,1;0rad)
  Refine = true
  Tool = -> Cylinder065
note: 5 file-system paths scrubbed to <path> (originals preserved in the JSON sidecar)
